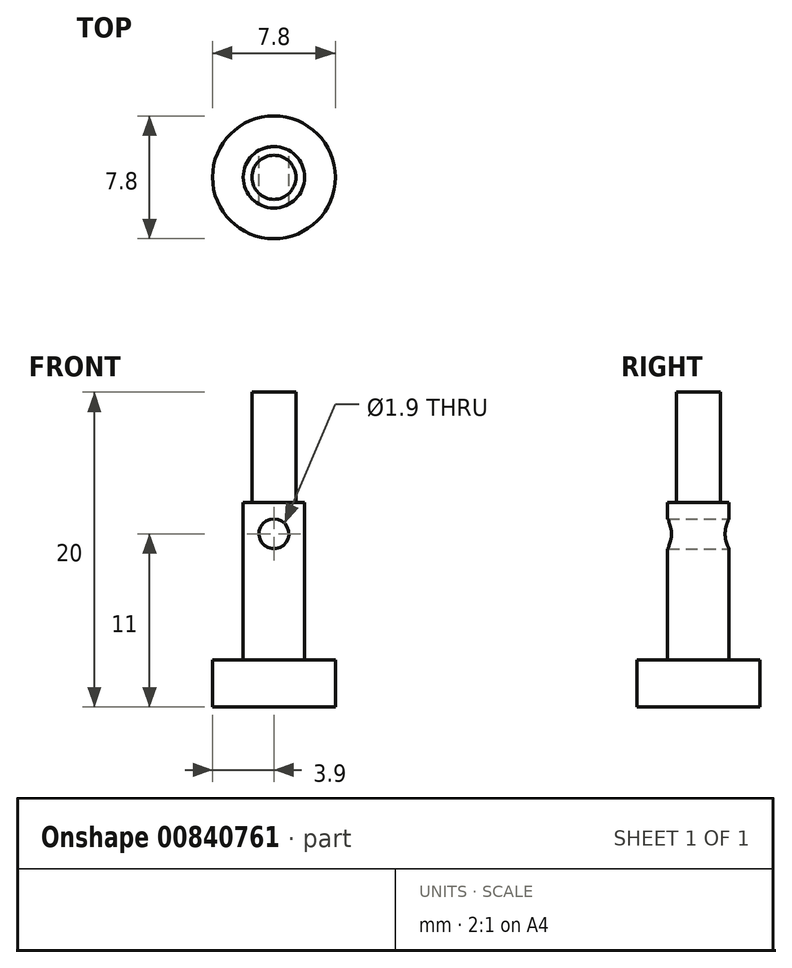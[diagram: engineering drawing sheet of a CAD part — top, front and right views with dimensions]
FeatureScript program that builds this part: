
annotation { "Feature Type Name" : "Feature", "Feature Type Description" : "" }
export const myFeature = defineFeature(function(context is Context, id is Id, definition is map)
    precondition{}
    {
        {
            var Q0;
            Q0=qCreatedBy(makeId("Top.planeOp"),FACE);
            var sketch = newSketch(context, id + "F0", { "sketchPlane" : qUnion([Q0])});
            skCircle(sketch, "E0", {"center": v(0, 0) * mm, "radius": 3.9 * mm});
            skSolve(sketch);
        }
        {
            var Q0;
            Q0 = qSketchRegion(id + "F0", true);
            extrude(context, id + "F1", {"entities" : qUnion([Q0]), "depth" : 3 * mm, "offsetDistance" : 25 * mm});
        }
        {
            var Q0;
            Q0=qCreatedBy(makeId("Top.planeOp"),FACE);
            cPlane(context, id + "F2", {"entities" : qUnion([Q0]), "cplaneType" : CPlaneType.OFFSET, "offset" : 3 * mm, "width" : 150 * mm, "height" : 150 * mm});
        }
        {
            var Q0;
            Q0=qCreatedBy(id+"F2.planeOp",FACE);
            var sketch = newSketch(context, id + "F3", { "sketchPlane" : qUnion([Q0])});
            skCircle(sketch, "E1", {"center": v(0, 0) * mm, "radius": 1.95 * mm});
            skSolve(sketch);
        }
        {
            var Q0;
            Q0 = qSketchRegion(id + "F3", true);
            extrude(context, id + "F4", {"entities" : qUnion([Q0]), "operationType" : NewBodyOperationType.ADD, "depth" : 10 * mm, "offsetDistance" : 25 * mm});
        }
        {
            var Q0;
            Q0=qCreatedBy(makeId("Front.planeOp"),FACE);
            var sketch = newSketch(context, id + "F5", { "sketchPlane" : qUnion([Q0])});
            skCircle(sketch, "E2", {"center": v(0, 11) * mm, "radius": 0.95 * mm});
            skSolve(sketch);
        }
        {
            var Q0;
            Q0=qCreatedBy(id+"F2.planeOp",FACE);
            cPlane(context, id + "F6", {"entities" : qUnion([Q0]), "cplaneType" : CPlaneType.OFFSET, "offset" : 10 * mm, "width" : 150 * mm, "height" : 150 * mm});
        }
        {
            var Q0;
            Q0=qCreatedBy(id+"F6.planeOp",FACE);
            var sketch = newSketch(context, id + "F7", { "sketchPlane" : qUnion([Q0])});
            skCircle(sketch, "E3", {"center": v(0, 0) * mm, "radius": 1.4 * mm});
            skSolve(sketch);
        }
        {
            var Q0;
            Q0 = qSketchRegion(id + "F7", true);
            extrude(context, id + "F8", {"entities" : qUnion([Q0]), "operationType" : NewBodyOperationType.ADD, "depth" : 7 * mm, "offsetDistance" : 25 * mm});
        }
        {
            var Q0;
            Q0 = qSketchRegion(id + "F5", true);
            extrude(context, id + "F9", {"entities" : qUnion([Q0]), "operationType" : NewBodyOperationType.REMOVE, "depth" : 4.8 * mm, "offsetDistance" : 25 * mm});
        }
        {
            var Q0;
            Q0 = qSketchRegion(id + "F5", true);
            extrude(context, id + "F10", {"entities" : qUnion([Q0]), "operationType" : NewBodyOperationType.REMOVE, "oppositeDirection" : true, "depth" : 4.8 * mm, "offsetDistance" : 25 * mm});
        }
    });
